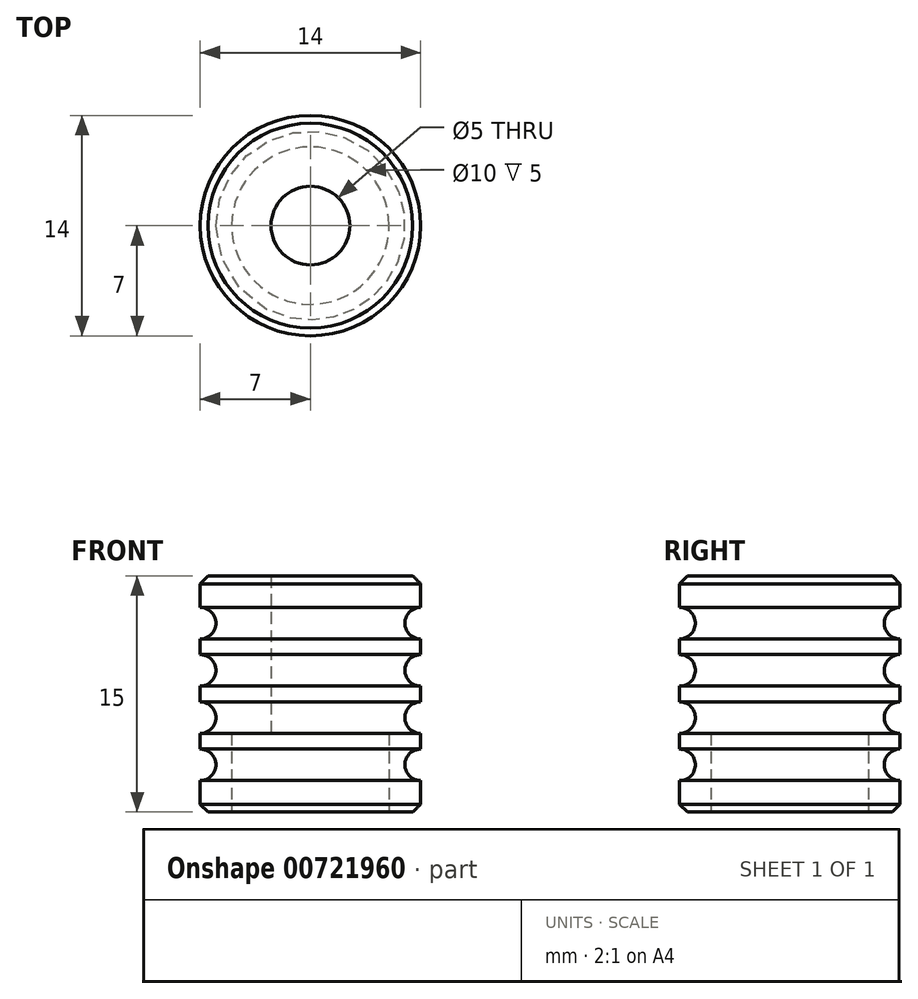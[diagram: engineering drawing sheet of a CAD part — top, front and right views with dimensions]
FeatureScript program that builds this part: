
annotation { "Feature Type Name" : "Feature", "Feature Type Description" : "" }
export const myFeature = defineFeature(function(context is Context, id is Id, definition is map)
    precondition{}
    {
        {
            var Q0;
            Q0=qCreatedBy(makeId("Top.planeOp"),FACE);
            var sketch = newSketch(context, id + "F0", { "sketchPlane" : qUnion([Q0])});
            skCircle(sketch, "E0", {"center": v(0, 0) * mm, "radius": 2.5 * mm});
            skCircle(sketch, "E1", {"center": v(0, 0) * mm, "radius": 7 * mm});
            skSolve(sketch);
        }
        {
            var Q0;
            Q0 = qSketchRegion(id + "F0", true);
            extrude(context, id + "F1", {"entities" : qUnion([Q0]), "depth" : 15 * mm, "offsetDistance" : 25 * mm});
        }
        {
            var Q0;
            Q0=makeQuery(id+"F1.opExtrude","CAP_FACE",FACE,{"disambiguationData":[OSD([sQuery(id+"F0.wireOp",EDGE,"E0"),sQuery(id+"F0.wireOp",EDGE,"E1")])],"isStart":true});
            var sketch = newSketch(context, id + "F2", { "sketchPlane" : qUnion([Q0])});
            skCircle(sketch, "E2", {"center": v(0, 0) * mm, "radius": 5 * mm});
            skSolve(sketch);
        }
        {
            var Q0;
            Q0 = qSketchRegion(id + "F2", true);
            extrude(context, id + "F3", {"entities" : qUnion([Q0]), "operationType" : NewBodyOperationType.REMOVE, "oppositeDirection" : true, "depth" : 5 * mm, "offsetDistance" : 25 * mm});
        }
        {
            var Q0;
            Q0=makeQuery(id+"F1.opExtrude","CAP_EDGE",EDGE,{"disambiguationData":[OSD([sQuery(id+"F0.wireOp",EDGE,"E1")])],"isStart":false});
            var Q1;
            Q1=makeQuery(id+"F1.opExtrude","CAP_EDGE",EDGE,{"disambiguationData":[OSD([sQuery(id+"F0.wireOp",EDGE,"E1")])],"isStart":true});
            chamfer(context, id + "F4", {"entities" : qUnion([Q0, Q1]), "width" : .5 * mm, "tangentPropagation" : true});
        }
        {
            var Q0;
            Q0=qCreatedBy(makeId("Right.planeOp"),FACE);
            var sketch = newSketch(context, id + "F5", { "sketchPlane" : qUnion([Q0])});
            skLineSegment(sketch, "E3", {"start": v(7, 17.2) * mm, "end": v(7, -7.55) * mm, "construction": true});
            skCircle(sketch, "E4", {"center": v(7, 12) * mm, "radius": 1 * mm});
            skCircle(sketch, "E5", {"center": v(7, 9) * mm, "radius": 1 * mm});
            skCircle(sketch, "E6", {"center": v(7, 6) * mm, "radius": 1 * mm});
            skCircle(sketch, "E7", {"center": v(7, 3) * mm, "radius": 1 * mm});
            skLineSegment(sketch, "E8", {"start": v(0, 20.27) * mm, "end": v(0, -5) * mm, "construction": true});
            skSolve(sketch);
        }
        {
            var Q0;
            Q0=makeQuery(id+"F5.imprint","IMPRINT",FACE,{"disambiguationData":[TD([[makeQuery(id+"F5.imprint","IMPRINT",EDGE,{"derivedFrom":sQuery(id+"F5.wireOp",EDGE,"E4")}),1.0]])]});
            var Q1;
            Q1=makeQuery(id+"F5.imprint","IMPRINT",FACE,{"disambiguationData":[TD([[makeQuery(id+"F5.imprint","IMPRINT",EDGE,{"derivedFrom":sQuery(id+"F5.wireOp",EDGE,"E5")}),1.0]])]});
            var Q2;
            Q2=makeQuery(id+"F5.imprint","IMPRINT",FACE,{"disambiguationData":[TD([[makeQuery(id+"F5.imprint","IMPRINT",EDGE,{"derivedFrom":sQuery(id+"F5.wireOp",EDGE,"E6")}),1.0]])]});
            var Q3;
            Q3=makeQuery(id+"F5.imprint","IMPRINT",FACE,{"disambiguationData":[TD([[makeQuery(id+"F5.imprint","IMPRINT",EDGE,{"derivedFrom":sQuery(id+"F5.wireOp",EDGE,"E7")}),1.0]])]});
            var Q4;
            Q4=sQuery(id+"F5.wireOp",EDGE,"E8");
            revolve(context, id + "F6", {"operationType" : NewBodyOperationType.REMOVE, "surfaceOperationType" : NewSurfaceOperationType.NEW, "entities" : qUnion([Q0, Q1, Q2, Q3]), "axis" : qUnion([Q4]), "revolveType" : RevolveType.FULL, "oppositeDirection" : true});
        }
    });
